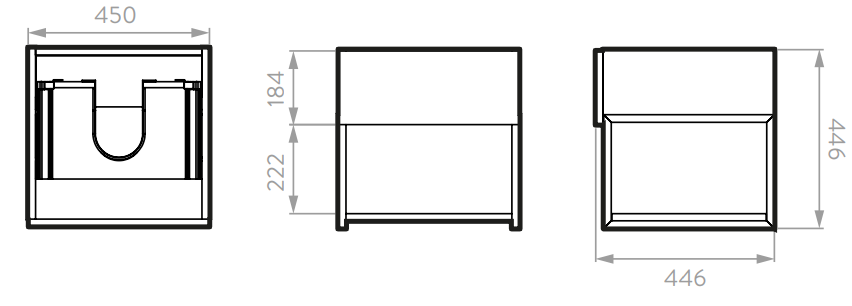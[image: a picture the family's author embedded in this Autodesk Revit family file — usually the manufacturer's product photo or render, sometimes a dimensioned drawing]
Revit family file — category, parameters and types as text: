
# Revit family: O34126491_ Mueble Fussion Plus 45 cm con Lavamanos
name_source: partatom
category: Aparatos sanitarios
units: mm (PartAtom-declared; Revit-internal decimal feet)

## family parameters
Anfitrión = Muro
Compartido = No
Corte con vacíos al cargar = No
Cota de conector redondo = Diámetro de uso
Número OmniClass = 23.45.00.00
Punto de cálculo de habitación = No
Siempre vertical = Sí
Tipo de pieza = Normal
Título OmniClass = Sanitary, Laundry, and Cleaning Equipment

## types (1)
- Type 1
    Alto = 1200 mm
    Alto Meson = 446 mm  [stored 1.46325 ft]
    Alto lavamanos = 120 mm  [stored 0.393701 ft]
    Ancho = 450 mm  [stored 1.47638 ft]
    Canto = PVC rígido 22 mm de calibre.
    Creado por = IDD
    Densidad = 18mm 659 kg./m^3. - 15mm 670 kg./m^3
    Descripción = Línea de Muebles Fussion Plus con repisa inferior expuesta e incrustaciones en aluminio que dan un toque moderno a tu baño!
    Estructura = Corona_Acero_Negro Mate
    Fabricante = Corona
    Fecha de creación = 31/07/2020
    Material = Corona_Madera_Taupe
    Modelo = Mueble Fussion Plus 45 cm con Lavamanos
    Peso Bruto aprox = 29.5 lb (13.4Kg)
    Peso Neto aprox = 24.3 lb (11Kg)
    Profundidad = 446 mm  [stored 1.46325 ft]
    Resistencia a la humedad = 8%
    Resistencia al rayado = 700 ciclos
    Textura = Taupé.
    URL = https://corona.co

note: [stored X ft] marks values corroborated as IEEE doubles in the binary element streams (Revit-internal decimal feet)

## geometry (parser evidence)
native form markers: Sweep x8
no freeform markers — native parametric forms only
